# Revit family: Chair-Soft_Seating-Allermuir-Open-A641FS
name_source: partatom
category: Furniture
revit_build: Autodesk Revit Architecture 2012 (Build: 20110309_2315(x64)
units: mm (PartAtom-declared; Revit-internal decimal feet)

## types (1)
- A643FS
    04 CSI = 12 51 00
    95 CSI = 12510
    Assembly Code = E2020200
    Brochure URL = http://www.allermuir.net
    CAD Blocks URL = http://www.allermuir.net
    Color Availability = See price list for material options
    Description = Footstool
    Fabric Spec Sheets = http://www.allermuir.net
    Glide Finish = Plastic - Allermuir - Black
    LEED Stats URL = http://www.allermuir.net
    Leg Base Height = 13 1/2"
    Manufacturer = Allermuir
    Manufacturer Fax = (419) 887 5805
    Model = A641FS
    Overall Depth = 20 13/128"
    Overall Height = 17 1/2"
    Overall Width = 21 179/256"
    Plugin Data URL = http://products.ecoscorecard.com
    Pricing URL = http://www.allermuir.net
    Product Line = Open
    Product Page URL = http://www.allermuir.net
    Seat = Fabric - Allermuir - Silcoates
    Specifications URL = http://www.allermuir.net
    Stand = Metal - Allermuir - Chrome - Polished
    Subcategory = Soft Seating
    URL = http://www.allermuir.net
    Weight = 15.0 lb
    White Plastic Back Membrane = No
    ecoScorecard Product Page = http://products.ecoscorecard.com
    ecoScorecard_data = http://thesenatorgroup.ecoscorecard.com

## geometry (parser evidence)
native form markers: Blend x3, Sweep x7
no freeform markers — native parametric forms only
